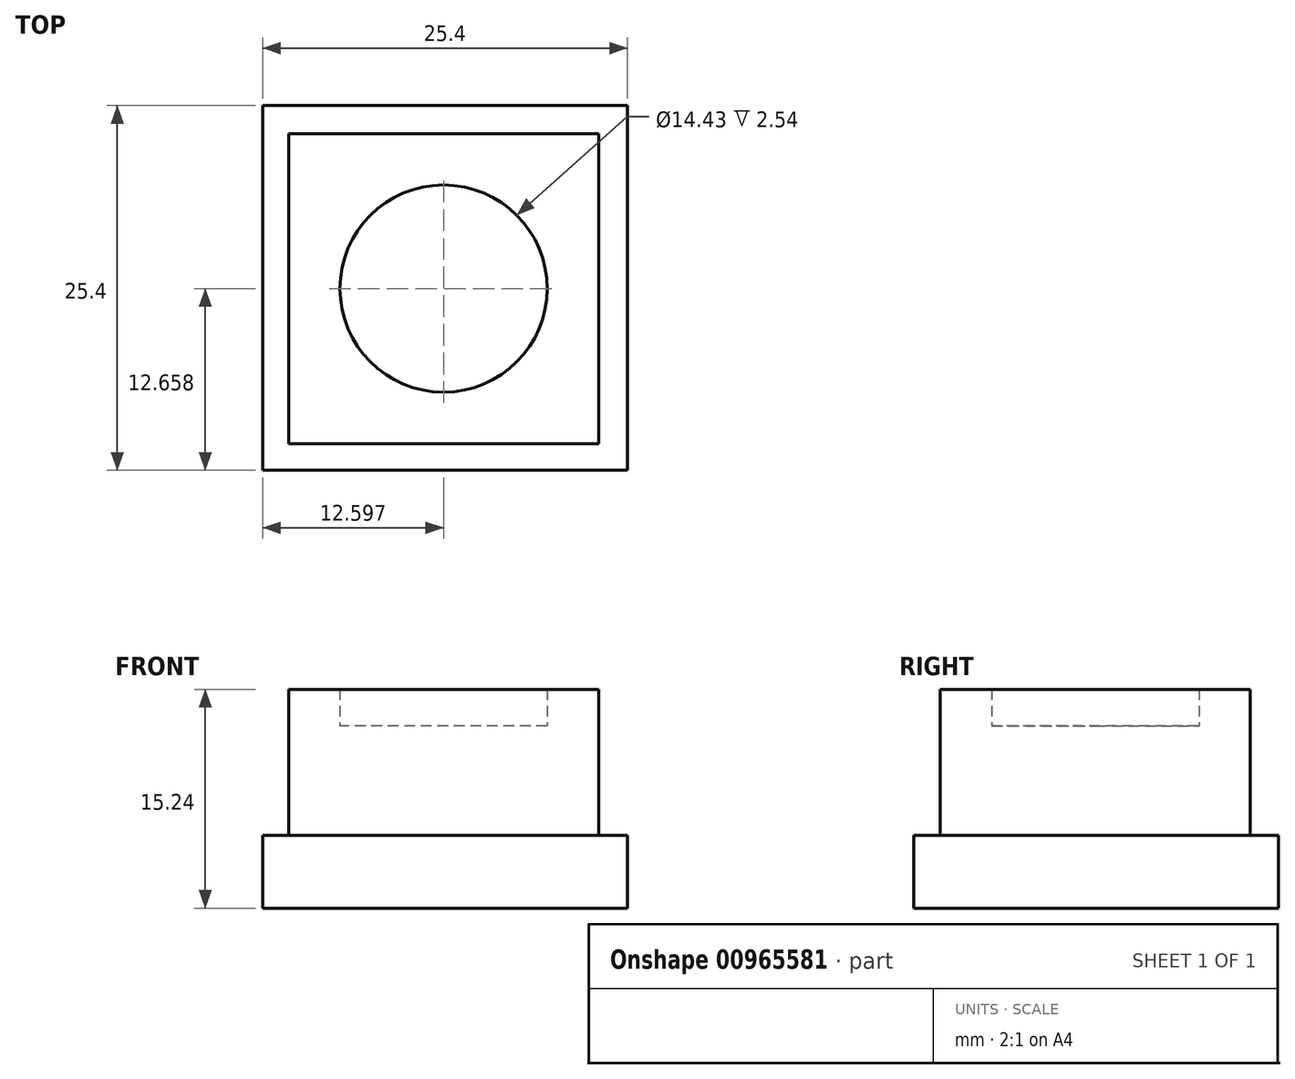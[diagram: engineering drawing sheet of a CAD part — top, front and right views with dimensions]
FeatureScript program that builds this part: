
annotation { "Feature Type Name" : "Feature", "Feature Type Description" : "" }
export const myFeature = defineFeature(function(context is Context, id is Id, definition is map)
    precondition{}
    {
        {
            var Q0;
            Q0=qCreatedBy(makeId("Top.planeOp"),FACE);
            var sketch = newSketch(context, id + "F0", { "sketchPlane" : qUnion([Q0])});
            skLineSegment(sketch, "E0.bottom", {"start": v(-51.1, 25.18) * mm, "end": v(-25.7, 25.18) * mm});
            skLineSegment(sketch, "E0.top", {"start": v(-51.1, -0.22) * mm, "end": v(-25.7, -0.22) * mm});
            skLineSegment(sketch, "E0.left", {"start": v(-51.1, 25.18) * mm, "end": v(-51.1, -0.22) * mm});
            skLineSegment(sketch, "E0.right", {"start": v(-25.7, 25.18) * mm, "end": v(-25.7, -0.22) * mm});
            skCircle(sketch, "E1", {"center": v(-38.5, 12.44) * mm, "radius": 7.22 * mm});
            skLineSegment(sketch, "E2.bottom", {"start": v(-27.7, 1.64) * mm, "end": v(-49.29, 1.64) * mm});
            skLineSegment(sketch, "E2.top", {"start": v(-27.7, 23.23) * mm, "end": v(-49.29, 23.23) * mm});
            skLineSegment(sketch, "E2.left", {"start": v(-27.7, 1.64) * mm, "end": v(-27.7, 23.23) * mm});
            skLineSegment(sketch, "E2.right", {"start": v(-49.29, 1.64) * mm, "end": v(-49.29, 23.23) * mm});
            skSolve(sketch);
        }
        {
            var Q0;
            Q0 = qSketchRegion(id + "F0", true);
            extrude(context, id + "F1", {"entities" : qUnion([Q0]), "depth" : 5.08 * mm, "offsetDistance" : 25.4 * mm});
        }
        {
            var Q0;
            Q0=makeQuery(id+"F0.imprint","IMPRINT",FACE,{"disambiguationData":[TD([[makeQuery(id+"F0.imprint","IMPRINT",EDGE,{"derivedFrom":sQuery(id+"F0.wireOp",EDGE,"E1")}),-1.0]])]});
            extrude(context, id + "F2", {"entities" : qUnion([Q0]), "operationType" : NewBodyOperationType.ADD, "depth" : 15.24 * mm, "offsetDistance" : 25.4 * mm});
        }
        {
            var Q0;
            Q0=makeQuery(id+"F0.imprint","IMPRINT",FACE,{"disambiguationData":[TD([[makeQuery(id+"F0.imprint","IMPRINT",EDGE,{"derivedFrom":sQuery(id+"F0.wireOp",EDGE,"E1")}),1.0]])]});
            extrude(context, id + "F3", {"entities" : qUnion([Q0]), "operationType" : NewBodyOperationType.ADD, "depth" : 12.7 * mm, "offsetDistance" : 25.4 * mm});
        }
    });
